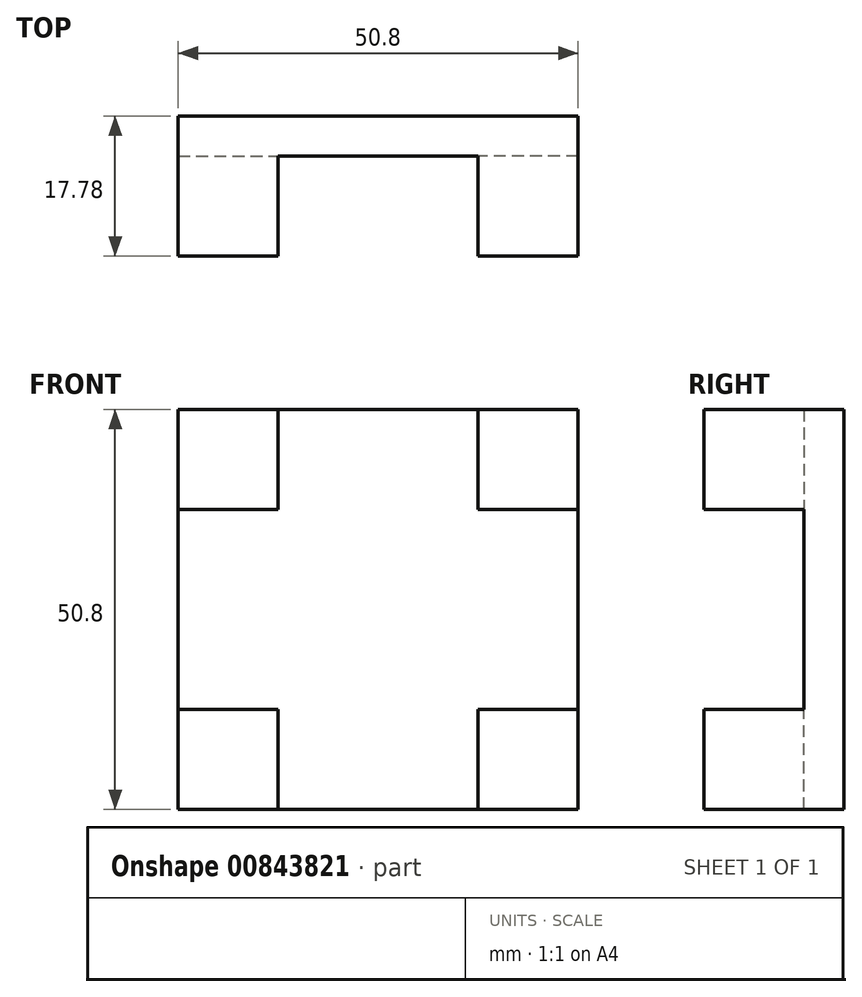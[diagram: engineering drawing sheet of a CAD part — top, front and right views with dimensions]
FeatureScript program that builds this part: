
annotation { "Feature Type Name" : "Feature", "Feature Type Description" : "" }
export const myFeature = defineFeature(function(context is Context, id is Id, definition is map)
    precondition{}
    {
        {
            var Q0;
            Q0=qCreatedBy(makeId("Front.planeOp"),FACE);
            var sketch = newSketch(context, id + "F0", { "sketchPlane" : qUnion([Q0])});
            skLineSegment(sketch, "E0.bottom", {"start": v(-980.88, 123) * mm, "end": v(-930.08, 123) * mm});
            skLineSegment(sketch, "E0.top", {"start": v(-980.88, 72.2) * mm, "end": v(-930.08, 72.2) * mm});
            skLineSegment(sketch, "E0.left", {"start": v(-980.88, 123) * mm, "end": v(-980.88, 72.2) * mm});
            skLineSegment(sketch, "E0.right", {"start": v(-930.08, 123) * mm, "end": v(-930.08, 72.2) * mm});
            skSolve(sketch);
        }
        {
            var Q0;
            Q0=makeQuery(id+"F0.imprint","IMPRINT",FACE,{"disambiguationData":[TD([[makeQuery(id+"F0.imprint","IMPRINT",EDGE,{"derivedFrom":sQuery(id+"F0.wireOp",EDGE,"E0.bottom")}),-1.0]])]});
            extrude(context, id + "F1", {"entities" : qUnion([Q0]), "depth" : 5.08 * mm, "offsetDistance" : 25.4 * mm});
        }
        {
            var Q0;
            Q0=makeQuery(id+"F1.opExtrude","CAP_FACE",FACE,{"disambiguationData":[OSD([sQuery(id+"F0.wireOp",EDGE,"E0.bottom"),sQuery(id+"F0.wireOp",EDGE,"E0.top"),sQuery(id+"F0.wireOp",EDGE,"E0.left"),sQuery(id+"F0.wireOp",EDGE,"E0.right")])],"isStart":false});
            var sketch = newSketch(context, id + "F2", { "sketchPlane" : qUnion([Q0])});
            skLineSegment(sketch, "E1.bottom", {"start": v(-980.88, 123) * mm, "end": v(-968.18, 123) * mm});
            skLineSegment(sketch, "E1.top", {"start": v(-980.88, 110.3) * mm, "end": v(-968.18, 110.3) * mm});
            skLineSegment(sketch, "E1.left", {"start": v(-980.88, 123) * mm, "end": v(-980.88, 110.3) * mm});
            skLineSegment(sketch, "E1.right", {"start": v(-968.18, 123) * mm, "end": v(-968.18, 110.3) * mm});
            skLineSegment(sketch, "E2.bottom", {"start": v(-930.08, 123) * mm, "end": v(-942.78, 123) * mm});
            skLineSegment(sketch, "E2.top", {"start": v(-930.08, 110.3) * mm, "end": v(-942.78, 110.3) * mm});
            skLineSegment(sketch, "E2.left", {"start": v(-930.08, 123) * mm, "end": v(-930.08, 110.3) * mm});
            skLineSegment(sketch, "E2.right", {"start": v(-942.78, 123) * mm, "end": v(-942.78, 110.3) * mm});
            skLineSegment(sketch, "E3.bottom", {"start": v(-980.88, 72.2) * mm, "end": v(-968.18, 72.2) * mm});
            skLineSegment(sketch, "E3.top", {"start": v(-980.88, 84.9) * mm, "end": v(-968.18, 84.9) * mm});
            skLineSegment(sketch, "E3.left", {"start": v(-980.88, 72.2) * mm, "end": v(-980.88, 84.9) * mm});
            skLineSegment(sketch, "E3.right", {"start": v(-968.18, 72.2) * mm, "end": v(-968.18, 84.9) * mm});
            skLineSegment(sketch, "E4.bottom", {"start": v(-930.08, 72.2) * mm, "end": v(-942.78, 72.2) * mm});
            skLineSegment(sketch, "E4.top", {"start": v(-930.08, 84.9) * mm, "end": v(-942.78, 84.9) * mm});
            skLineSegment(sketch, "E4.left", {"start": v(-930.08, 72.2) * mm, "end": v(-930.08, 84.9) * mm});
            skLineSegment(sketch, "E4.right", {"start": v(-942.78, 72.2) * mm, "end": v(-942.78, 84.9) * mm});
            skSolve(sketch);
        }
        {
            var Q0;
            Q0 = qSketchRegion(id + "F2", true);
            extrude(context, id + "F3", {"entities" : qUnion([Q0]), "operationType" : NewBodyOperationType.ADD, "depth" : 12.7 * mm, "offsetDistance" : 25.4 * mm});
        }
    });
